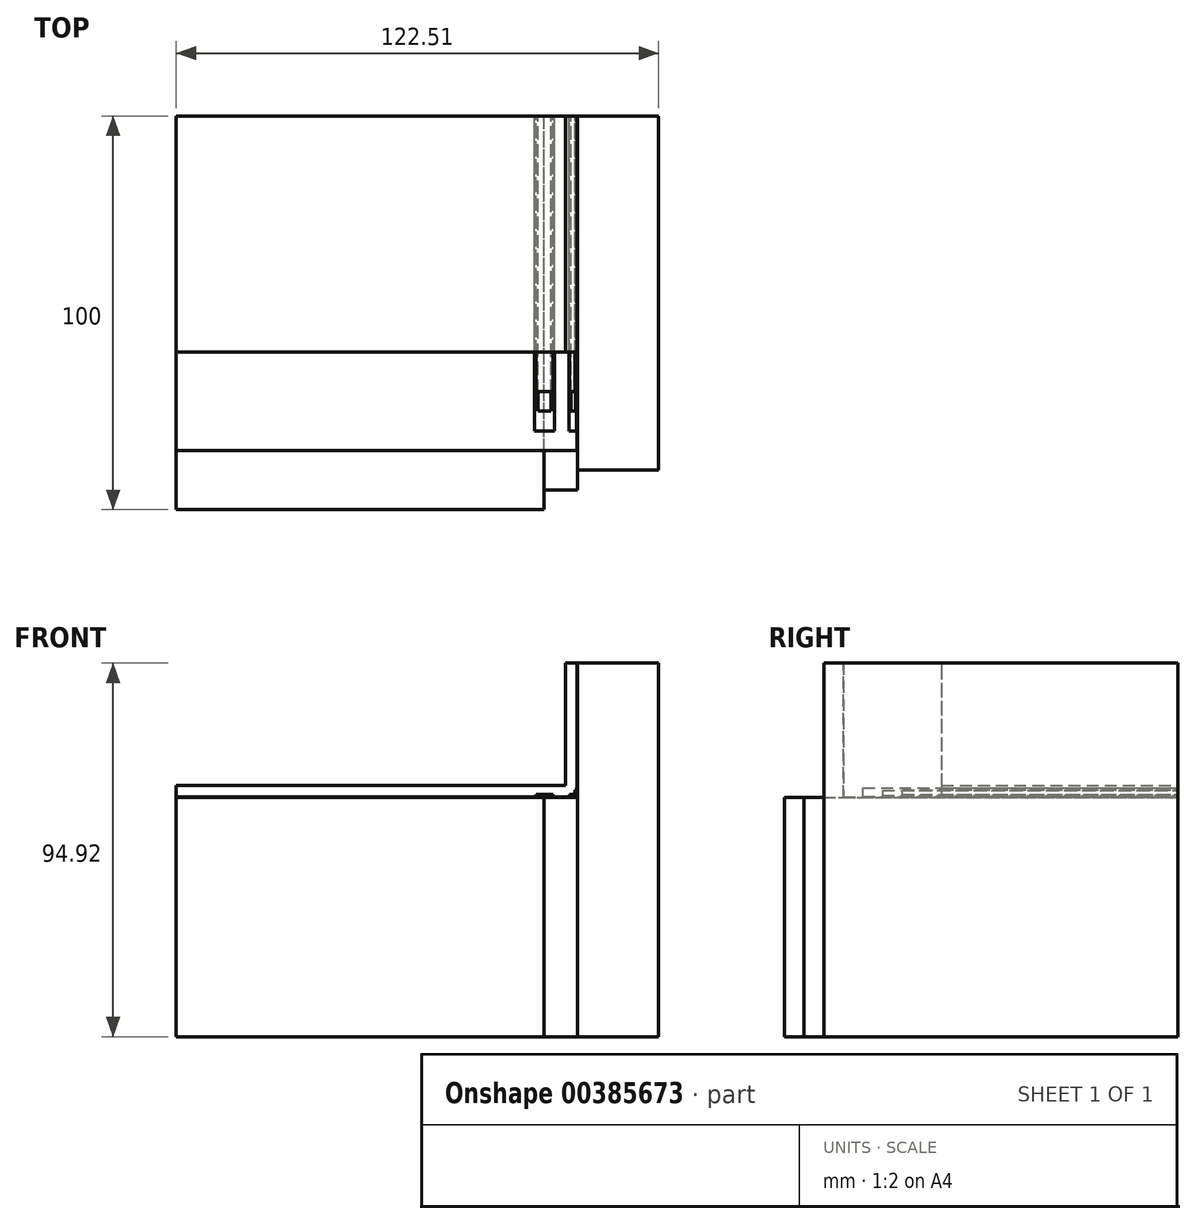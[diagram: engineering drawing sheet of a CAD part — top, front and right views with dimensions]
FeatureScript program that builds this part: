
annotation { "Feature Type Name" : "Feature", "Feature Type Description" : "" }
export const myFeature = defineFeature(function(context is Context, id is Id, definition is map)
    precondition{}
    {
        {
            var Q0;
            Q0=qCreatedBy(makeId("Front.planeOp"),FACE);
            var sketch = newSketch(context, id + "F0", { "sketchPlane" : qUnion([Q0])});
            skLineSegment(sketch, "E0", {"start": v(-96.96, 19.18) * mm, "end": v(-96.96, -41.61) * mm});
            skLineSegment(sketch, "E1", {"start": v(-96.96, -41.61) * mm, "end": v(-3.51, -41.61) * mm});
            skLineSegment(sketch, "E2", {"start": v(-3.51, -41.61) * mm, "end": v(-3.51, 19.18) * mm});
            skLineSegment(sketch, "E3", {"start": v(-3.51, 19.18) * mm, "end": v(-96.96, 19.18) * mm});
            skLineSegment(sketch, "E4", {"start": v(-3.51, 19.18) * mm, "end": v(5, 19.18) * mm});
            skLineSegment(sketch, "E5", {"start": v(5, 19.18) * mm, "end": v(5, -41.61) * mm});
            skLineSegment(sketch, "E6", {"start": v(5, -41.61) * mm, "end": v(-3.51, -41.61) * mm});
            skLineSegment(sketch, "E7", {"start": v(5, 53.3) * mm, "end": v(5, 19.18) * mm});
            skLineSegment(sketch, "E8", {"start": v(5, 53.3) * mm, "end": v(25.55, 53.3) * mm});
            skLineSegment(sketch, "E9", {"start": v(25.55, 53.3) * mm, "end": v(25.55, -41.61) * mm});
            skLineSegment(sketch, "E10", {"start": v(25.55, -41.61) * mm, "end": v(5, -41.61) * mm});
            skLineSegment(sketch, "E11", {"start": v(-96.96, 19.18) * mm, "end": v(-96.96, 19.28) * mm});
            skLineSegment(sketch, "E12", {"start": v(-96.96, 19.28) * mm, "end": v(4.9, 19.28) * mm});
            skLineSegment(sketch, "E13", {"start": v(4.9, 19.28) * mm, "end": v(4.9, 53.3) * mm});
            skLineSegment(sketch, "E14", {"start": v(4.9, 53.3) * mm, "end": v(5, 53.3) * mm});
            skLineSegment(sketch, "E15", {"start": v(4.9, 19.28) * mm, "end": v(4.9, 19.18) * mm, "construction": true});
            skLineSegment(sketch, "E16", {"start": v(-96.96, 19.28) * mm, "end": v(-96.96, 22.28) * mm});
            skLineSegment(sketch, "E17", {"start": v(-96.96, 22.28) * mm, "end": v(1.9, 22.28) * mm});
            skLineSegment(sketch, "E18", {"start": v(1.9, 22.28) * mm, "end": v(1.9, 53.3) * mm});
            skLineSegment(sketch, "E19", {"start": v(1.9, 53.3) * mm, "end": v(4.9, 53.3) * mm});
            skLineSegment(sketch, "E20", {"start": v(1.9, 22.28) * mm, "end": v(1.9, 19.28) * mm, "construction": true});
            skLineSegment(sketch, "E21", {"start": v(-5.9, 19.28) * mm, "end": v(-5.9, 19.48) * mm});
            skLineSegment(sketch, "E22", {"start": v(-5.9, 19.48) * mm, "end": v(-0.83, 19.48) * mm});
            skLineSegment(sketch, "E23", {"start": v(-0.83, 19.48) * mm, "end": v(-0.83, 19.28) * mm});
            skLineSegment(sketch, "E24", {"start": v(-5, 19.48) * mm, "end": v(-5, 19.68) * mm});
            skLineSegment(sketch, "E25", {"start": v(-5, 19.68) * mm, "end": v(-1.75, 19.68) * mm});
            skLineSegment(sketch, "E26", {"start": v(-1.75, 19.68) * mm, "end": v(-1.75, 19.48) * mm});
            skLineSegment(sketch, "E27", {"start": v(-5.6, 19.48) * mm, "end": v(-5.6, 19.88) * mm});
            skLineSegment(sketch, "E28", {"start": v(-5.6, 19.88) * mm, "end": v(-1.28, 19.88) * mm});
            skLineSegment(sketch, "E29", {"start": v(-1.28, 19.88) * mm, "end": v(-1.28, 19.48) * mm});
            skLineSegment(sketch, "E30", {"start": v(2.8, 19.28) * mm, "end": v(2.8, 19.48) * mm});
            skLineSegment(sketch, "E31", {"start": v(2.8, 19.48) * mm, "end": v(4.7, 19.48) * mm});
            skLineSegment(sketch, "E32", {"start": v(4.7, 19.48) * mm, "end": v(4.7, 21.6) * mm});
            skLineSegment(sketch, "E33", {"start": v(4.7, 21.6) * mm, "end": v(4.9, 21.6) * mm});
            skLineSegment(sketch, "E34", {"start": v(3.32, 19.48) * mm, "end": v(3.32, 19.68) * mm});
            skLineSegment(sketch, "E35", {"start": v(3.32, 19.68) * mm, "end": v(4.5, 19.68) * mm});
            skLineSegment(sketch, "E36", {"start": v(4.5, 19.68) * mm, "end": v(4.5, 20.96) * mm});
            skLineSegment(sketch, "E37", {"start": v(4.5, 20.96) * mm, "end": v(4.7, 20.96) * mm});
            skLineSegment(sketch, "E38", {"start": v(3.02, 19.48) * mm, "end": v(3.02, 19.88) * mm});
            skLineSegment(sketch, "E39", {"start": v(3.02, 19.88) * mm, "end": v(4.3, 19.88) * mm});
            skLineSegment(sketch, "E40", {"start": v(4.3, 19.88) * mm, "end": v(4.3, 21.1) * mm});
            skLineSegment(sketch, "E41", {"start": v(4.3, 21.1) * mm, "end": v(4.7, 21.1) * mm});
            skLineSegment(sketch, "E42", {"start": v(4.7, 19.48) * mm, "end": v(4.9, 19.48) * mm, "construction": true});
            skLineSegment(sketch, "E43", {"start": v(4.5, 19.68) * mm, "end": v(4.7, 19.68) * mm, "construction": true});
            skLineSegment(sketch, "E44", {"start": v(4.3, 19.88) * mm, "end": v(4.5, 19.88) * mm, "construction": true});
            skLineSegment(sketch, "E45", {"start": v(4.5, 20.96) * mm, "end": v(4.5, 21.1) * mm, "construction": true});
            skLineSegment(sketch, "E46", {"start": v(3.32, 19.68) * mm, "end": v(3.32, 19.88) * mm, "construction": true});
            skSolve(sketch);
        }
        {
            var Q0;
            Q0=makeQuery(id+"F0.imprint","IMPRINT",FACE,{"disambiguationData":[TD([[makeQuery(id+"F0.imprint","IMPRINT",EDGE,{"derivedFrom":sQuery(id+"F0.wireOp",EDGE,"E0")}),1.0]])]});
            extrude(context, id + "F1", {"entities" : qUnion([Q0]), "depth" : 100 * mm});
        }
        {
            var Q0;
            Q0=makeQuery(id+"F0.imprint","IMPRINT",FACE,{"disambiguationData":[TD([[makeQuery(id+"F0.imprint","IMPRINT",EDGE,{"derivedFrom":sQuery(id+"F0.wireOp",EDGE,"E2")}),-1.0]])]});
            extrude(context, id + "F2", {"entities" : qUnion([Q0]), "depth" : 95 * mm});
        }
        {
            var Q0;
            Q0=makeQuery(id+"F0.imprint","IMPRINT",FACE,{"disambiguationData":[TD([[makeQuery(id+"F0.imprint","IMPRINT",EDGE,{"derivedFrom":sQuery(id+"F0.wireOp",EDGE,"E5")}),1.0]])]});
            extrude(context, id + "F3", {"entities" : qUnion([Q0]), "depth" : 90 * mm});
        }
        {
            var Q0;
            Q0=makeQuery(id+"F0.imprint","IMPRINT",FACE,{"disambiguationData":[TD([[makeQuery(id+"F0.imprint","IMPRINT",EDGE,{"derivedFrom":sQuery(id+"F0.wireOp",EDGE,"E3")}),-1.0]])]});
            extrude(context, id + "F4", {"entities" : qUnion([Q0]), "depth" : 85 * mm});
        }
        {
            var Q0;
            {var subQ3=sQuery(id+"F0.wireOp",EDGE,"E21");Q0=makeQuery(id+"F0.imprint","IMPRINT",FACE,{"disambiguationData":[TD([[makeQuery(id+"F0.imprint","IMPRINT",EDGE,{"derivedFrom":subQ3}),-1.0]])]});}
            extrude(context, id + "F5", {"entities" : qUnion([Q0]), "depth" : 80 * mm});
        }
        {
            var Q0;
            {var subQ1=sQuery(id+"F0.wireOp",EDGE,"E30");Q0=makeQuery(id+"F0.imprint","IMPRINT",FACE,{"disambiguationData":[TD([[makeQuery(id+"F0.imprint","IMPRINT",EDGE,{"derivedFrom":subQ1}),-1.0]])]});}
            extrude(context, id + "F6", {"entities" : qUnion([Q0]), "depth" : 80 * mm});
        }
        {
            var Q0;
            {var subQ0=sQuery(id+"F0.wireOp",EDGE,"E24");Q0=makeQuery(id+"F0.imprint","IMPRINT",FACE,{"disambiguationData":[TD([[makeQuery(id+"F0.imprint","IMPRINT",EDGE,{"derivedFrom":subQ0}),-1.0]])]});}
            extrude(context, id + "F7", {"entities" : qUnion([Q0]), "depth" : 75 * mm});
        }
        {
            var Q0;
            {var subQ4=sQuery(id+"F0.wireOp",EDGE,"E34");Q0=makeQuery(id+"F0.imprint","IMPRINT",FACE,{"disambiguationData":[TD([[makeQuery(id+"F0.imprint","IMPRINT",EDGE,{"derivedFrom":subQ4}),-1.0]])]});}
            extrude(context, id + "F8", {"entities" : qUnion([Q0]), "depth" : 75 * mm});
        }
        {
            var Q0;
            {var subQ3=sQuery(id+"F0.wireOp",EDGE,"E24");Q0=makeQuery(id+"F0.imprint","IMPRINT",FACE,{"disambiguationData":[TD([[makeQuery(id+"F0.imprint","IMPRINT",EDGE,{"derivedFrom":subQ3}),1.0]])]});}
            extrude(context, id + "F9", {"entities" : qUnion([Q0]), "depth" : 70 * mm});
        }
        {
            var Q0;
            {var subQ0=sQuery(id+"F0.wireOp",EDGE,"E34");Q0=makeQuery(id+"F0.imprint","IMPRINT",FACE,{"disambiguationData":[TD([[makeQuery(id+"F0.imprint","IMPRINT",EDGE,{"derivedFrom":subQ0}),1.0]])]});}
            extrude(context, id + "F10", {"entities" : qUnion([Q0]), "depth" : 70 * mm});
        }
        {
            var Q0;
            {var subQ5=sQuery(id+"F0.wireOp",EDGE,"E16");Q0=makeQuery(id+"F0.imprint","IMPRINT",FACE,{"disambiguationData":[TD([[makeQuery(id+"F0.imprint","IMPRINT",EDGE,{"derivedFrom":subQ5}),-1.0]])]});}
            extrude(context, id + "F11", {"entities" : qUnion([Q0]), "depth" : 60 * mm});
        }
    });
